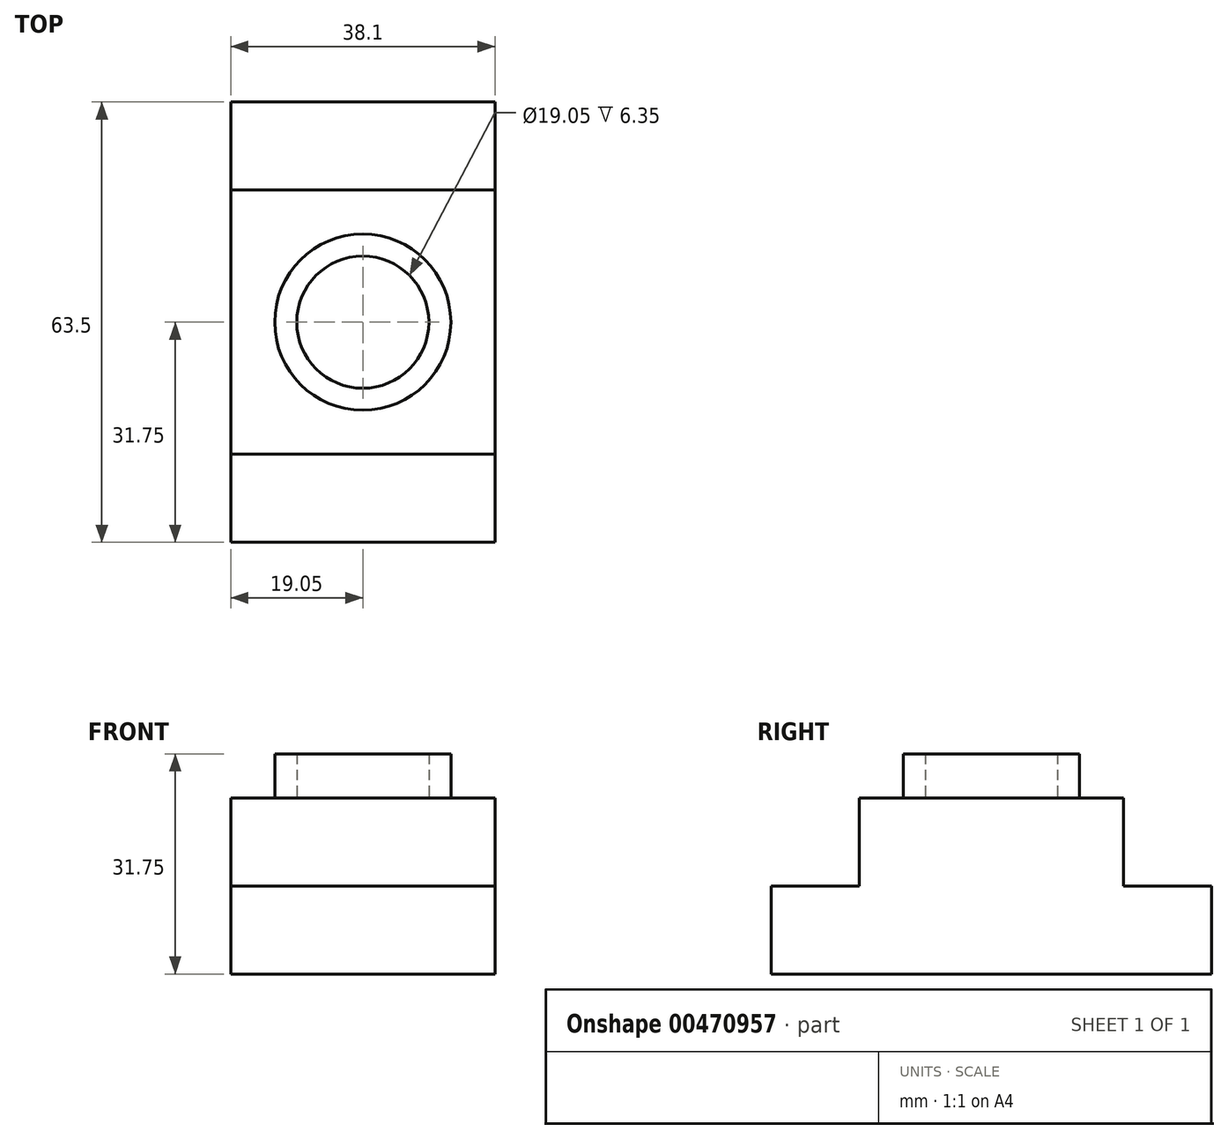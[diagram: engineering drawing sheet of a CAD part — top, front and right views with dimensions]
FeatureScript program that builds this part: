
annotation { "Feature Type Name" : "Feature", "Feature Type Description" : "" }
export const myFeature = defineFeature(function(context is Context, id is Id, definition is map)
    precondition{}
    {
        {
            var Q0;
            Q0=qCreatedBy(makeId("Right.planeOp"),FACE);
            var sketch = newSketch(context, id + "F0", { "sketchPlane" : qUnion([Q0])});
            skLineSegment(sketch, "E0", {"start": v(0, 0) * mm, "end": v(-31.75, 0) * mm});
            skLineSegment(sketch, "E1", {"start": v(-31.75, 0) * mm, "end": v(-31.75, 12.7) * mm});
            skLineSegment(sketch, "E2", {"start": v(-31.75, 12.7) * mm, "end": v(-19.05, 12.7) * mm});
            skLineSegment(sketch, "E3", {"start": v(-19.05, 12.7) * mm, "end": v(-19.05, 25.4) * mm});
            skLineSegment(sketch, "E4", {"start": v(-19.05, 25.4) * mm, "end": v(19.05, 25.4) * mm});
            skLineSegment(sketch, "E5", {"start": v(19.05, 25.4) * mm, "end": v(19.05, 12.7) * mm});
            skLineSegment(sketch, "E6", {"start": v(19.05, 12.7) * mm, "end": v(31.75, 12.7) * mm});
            skLineSegment(sketch, "E7", {"start": v(31.75, 12.7) * mm, "end": v(31.75, 0) * mm});
            skLineSegment(sketch, "E8", {"start": v(19.05, 12.7) * mm, "end": v(19.05, 12.7) * mm});
            skLineSegment(sketch, "E9", {"start": v(0, 0) * mm, "end": v(31.75, 0) * mm});
            skSolve(sketch);
        }
        {
            var Q0;
            Q0 = qSketchRegion(id + "F0", true);
            extrude(context, id + "F1", {"entities" : qUnion([Q0]), "depth" : 38.1 * mm});
        }
        {
            var Q0;
            Q0=makeQuery(id+"F1.opExtrude","SWEPT_FACE",FACE,{"disambiguationData":[OSD([sQuery(id+"F0.wireOp",EDGE,"E4")])]});
            var sketch = newSketch(context, id + "F2", { "sketchPlane" : qUnion([Q0])});
            skCircle(sketch, "E10", {"center": v(19.05, 0) * mm, "radius": 12.7 * mm});
            skPoint(sketch, "E10.centerSnap0", {"position": v(0, 0) * mm});
            skCircle(sketch, "E11", {"center": v(19.05, 0) * mm, "radius": 9.53 * mm});
            skSolve(sketch);
        }
        {
            var Q0;
            Q0 = qSketchRegion(id + "F2", true);
            extrude(context, id + "F3", {"entities" : qUnion([Q0]), "operationType" : NewBodyOperationType.ADD, "depth" : 6.35 * mm});
        }
    });
